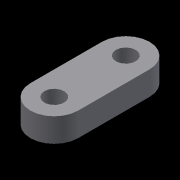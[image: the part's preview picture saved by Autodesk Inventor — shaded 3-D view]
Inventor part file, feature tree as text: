
AUTODESK INVENTOR PART (.ipt)
format: ipt  version: 2015 SP1 (Build 190203100, 203)  size: 82,944 bytes
history: native  units: mm
features: other x2, imported_body x1, extrude x1, hole x1
ambient origin geometry x8: Origin, YZ Plane, XZ Plane, XY Plane, X Axis, Y Axis, Z Axis, Center Point
bodies: Body1 (feature_tree)
feature tree (5):
  other  "VibroMount"
  other  "Main"
  imported_body  "Base"
  extrude  "BaseFeature"  Depth=6.0mm
  hole  "MountHolesFeature"  [1 undecoded]
note: 1 required parameter value undecoded (feature->parameter linkage not recoverable at this tier; creation-order binding heuristic only, values carry confidence <= 0.55)
